# Revit family: SIMES_S.1256W_Streamline
name_source: partatom
category: Lighting Fixtures
revit_build: Autodesk Revit 2016 (Build: 20150714_1515(x64)
units: mm (PartAtom-declared; Revit-internal decimal feet)

## family parameters
Cut with Voids When Loaded = No
Host = Face
Light Source = No
OmniClass Number = 23.80.70.14
OmniClass Title = Luminaries for External Lighting
Part Type = Normal
Room Calculation Point = No
Round Connector Dimension = Use Diameter
Shared = No

## types (1)
- SIMES_S.1256W_Streamline
    Approval mark = CE
    Assembly Code = D5020
    BIMobject category = Outside
    BIMobject category code = lighting-outside
    BIMobject main category = Lighting
    BIMobject main category code = lighting
    Brand url = http://www.simes.it
    Color Rendering Index = CRI 90
    Colour Temperature = 3000
    Control Gear = electronic transformer
    Default Elevation = 1219 mm
    Description = STREAMLINE PROJECTOR
Art. S.1256W
MODULES LED 3000K  230V CRI 90
Rated luminaire luminous flux: 4904lm
Rated input power: 74W
Luminaire efficacy: 66lm/W
Electronic ballast 220÷240V 50/60Hz
CE

Fixture available with integral DALI driver on request with surcharge.

PRODUCT TYPE
Wall mounted luminaire. IP rating IP 65
MATERIAL CHARACTERISTICS
Die-cast EN AB-47100 aluminium housing with high corrosion resistance. Stone wash surface treatment prior to painting process. A4 grade Stainless Steel screws with 2,5-3% molybdenum content which increases the resistance against corrosion. Pre treated Silicone Gaskets. Painting Process : 3 Step Process
1) Surface treatment with BONDERITE. A heavy metal free chemical surface treatment containing ceramic nano particles giving a cohesive, inorganic and highly dense protective coating. 2) PRE POLYMERIZATION a process of introducing an epoxy primer with excellent characteristics to the paint which also offers very high resistance to oxidation due to its Zinc content. 3) POLYMERIZATION a process with the application of polyester powder with high resistance against UV rays and harsh weather conditions. Resistance test protection for Marine applications for 1200h.  Mechanical resistance IK 07 Maximum load capacity --
LIGHTING PERFORMANCE
Clear toughened glass diffuser. LOR --. Compact electronic ballast to guarantee better lamp stability, lifetime and reduced energy consumption. Projector version: The sophisticated optics focuses the beam and makes the light comfortable by reducing the direct glare of the light source.
INSTALLATION AND MANTEINANCE
Streamline wall mounted allows three different beam settings: 0° - 5° - 10°. Streamline projector suitable with the bracket that allows a 180° product rotation.
WIRING
Luminaire suitable for single cable gland ( projector ) or single grommet ( wall ). Isolation: CLASS I . Available colours: Aluminium grey (cod.14). Weight: 6.9 Kg Glow Wire test: --
Lamp included.
This luminaire contains built-in LED modules with energy class: A, A+, A++. In case of damage or malfunction please contact the manufacturer to receive additional instructions on how to replace and relative spare parts to order. The LED modules cannot be handled in the luminaire by the end user (Regulation UE 874/2012).
LED circuit boards are engineered accordingly to actual Lumen Maintenance regulation (LM80) and Technical Memorandum (TM21) where uniformity and quality of light is 50.000 hours referred to L70  B20 Ta 25°C.Lifecycle refers to LED circuit boards only, all others components of the luminaire are excluded.
    Design country = Italy
    Edition number = 1
    Frequency = 50/60Hz
    IFC Classification = Light Fixture
    IK Rating = IK 07
    Lamp = LED
    Lamp Light Flux = 7920
    Lamp Power = 15,800000190734863
    Lamp count = 1
    Last Update = 08/11/2018 16:39:33
    Lifetime = 50000 L70 B20 Ta 25°C
    Light Output Ratio = 100
    Luminous efficacy = 66,3
    Manufacturer = SIMES
    Manufacturer country = Italy
    Manufacturer name = Simes
    Masterformat 2014 Code = 26 56 00
    Masterformat 2014 Description = Exterior Lighting
    Material main = Aluminium
    Material secondary = Glass
    Model = S.1256W
    Mounting Place = Ceiling
    Mounting Type = Surface mounted
    NBS Reference Code = 49
    NBS Reference Description = Luminaries And Lamps
    Nominal height = 44 mm  [stored 0.144357 ft]
    Nominal width = 977 mm  [stored 3.20538 ft]
    OmniClass Code = 23-35 47 11
    OmniClass Description = Lighting Fixture
    Product Group = projector
    Product Guid = 2a8a3b18-74a8-46b7-b9db-44669fabe994
    Product Name = Streamline projector
    Product SKU = STREAMLINE-PROJECTOR
    Product certification = http://www.simes.it
    Product data url = https://bimobject.com
    Product family = Projectors
    Product url = http://www.simes.it
    Protection Class = Protection class I
    Protection Degree = IP 65
    QR code = http://bimobject.com
    System Light Flux = 4904
    System Power = 74
    Technical description = http://www.simes.it
    Type Comments = SIMES S.p.A. - All rights reserved
    Type Image = streamline_proiettore2018.jpg
    UNSPSC Code = 3911
    URL = http://www.simes.it
    Uniclass 1.4 Code = YJ73
    Uniclass 1.4 Description = Luminaries and lamps
    Uniclass 2.0 Code = PR-49
    Uniclass 2.0 Description = Luminaries and lamps
    Uniclass 2015 Code = EF_70_80
    Uniclass 2015 Name = Lighting
    Uniformat II Code = D5020
    Uniformat II Description = Lighting & Branch Wiring
    Voltage = 220÷240V
    Wattage Comments = 84W
    Weight Net (Kg) = 4

note: [stored X ft] marks values corroborated as IEEE doubles in the binary element streams (Revit-internal decimal feet)

## geometry (parser evidence)
native form markers: Blend x2, Sweep x3
no freeform markers — native parametric forms only
